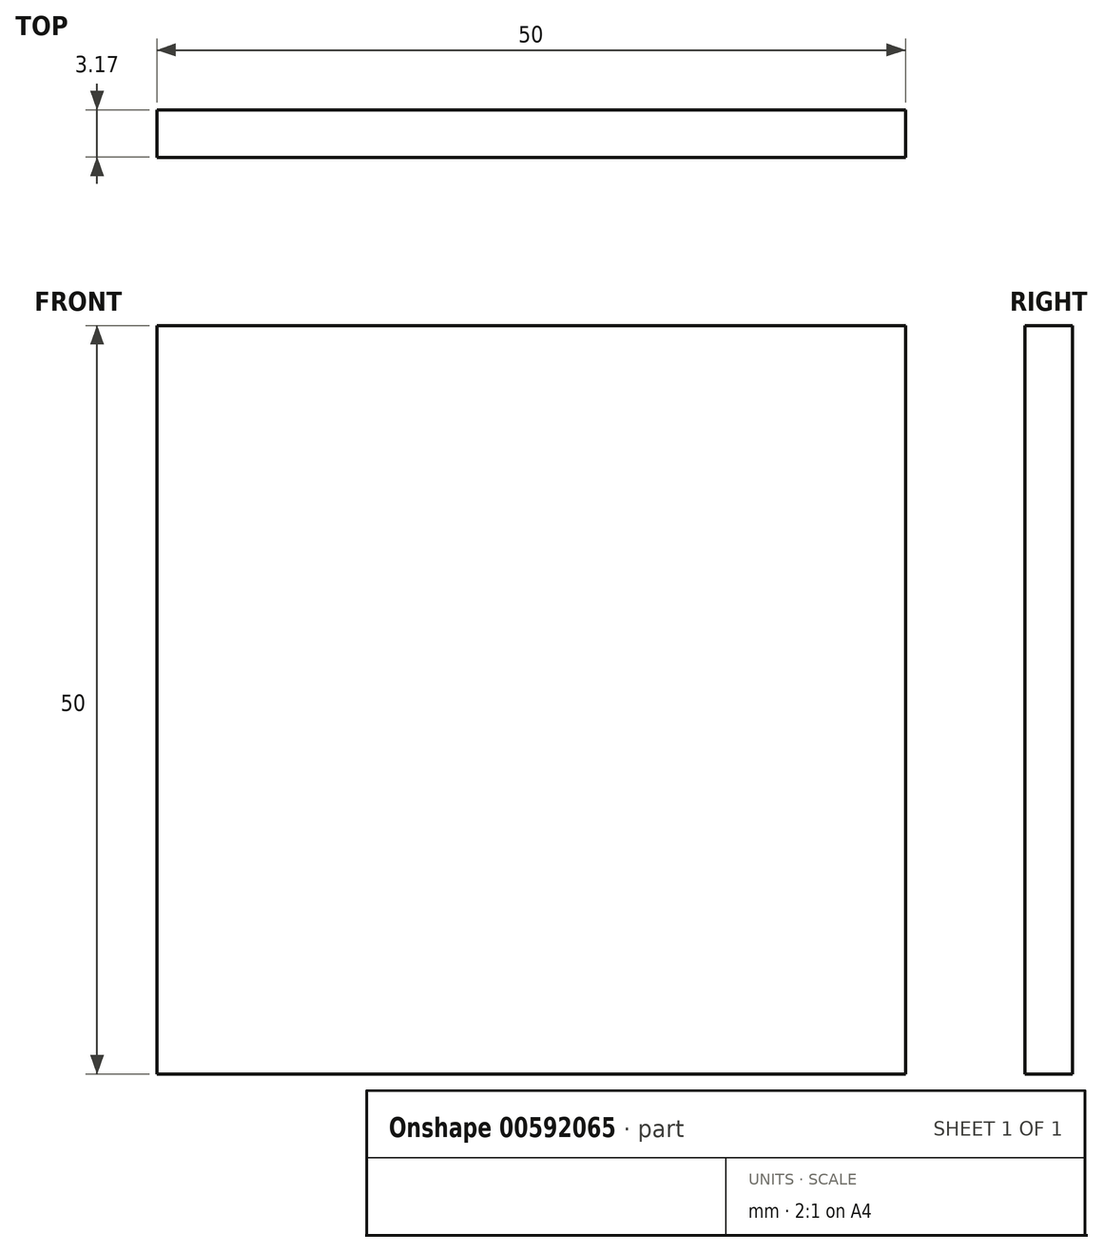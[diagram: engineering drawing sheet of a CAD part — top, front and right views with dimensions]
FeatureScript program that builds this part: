
annotation { "Feature Type Name" : "Feature", "Feature Type Description" : "" }
export const myFeature = defineFeature(function(context is Context, id is Id, definition is map)
    precondition{}
    {
        {
            var Q0;
            Q0=qCreatedBy(makeId("Front.planeOp"),FACE);
            var sketch = newSketch(context, id + "F0", { "sketchPlane" : qUnion([Q0])});
            skLineSegment(sketch, "E0.bottom", {"start": v(-25, 25) * mm, "end": v(25, 25) * mm});
            skLineSegment(sketch, "E0.top", {"start": v(-25, -25) * mm, "end": v(25, -25) * mm});
            skLineSegment(sketch, "E0.left", {"start": v(-25, 25) * mm, "end": v(-25, -25) * mm});
            skLineSegment(sketch, "E0.right", {"start": v(25, 25) * mm, "end": v(25, -25) * mm});
            skLineSegment(sketch, "E1", {"start": v(25, 0) * mm, "end": v(-25, 0) * mm, "construction": true});
            skLineSegment(sketch, "E2", {"start": v(0, 25) * mm, "end": v(0, -25) * mm, "construction": true});
            skSolve(sketch);
        }
        {
            var Q0;
            Q0 = qSketchRegion(id + "F0", true);
            extrude(context, id + "F1", {"entities" : qUnion([Q0]), "depth" : 3.17 * mm, "offsetDistance" : 25 * mm});
        }
    });
